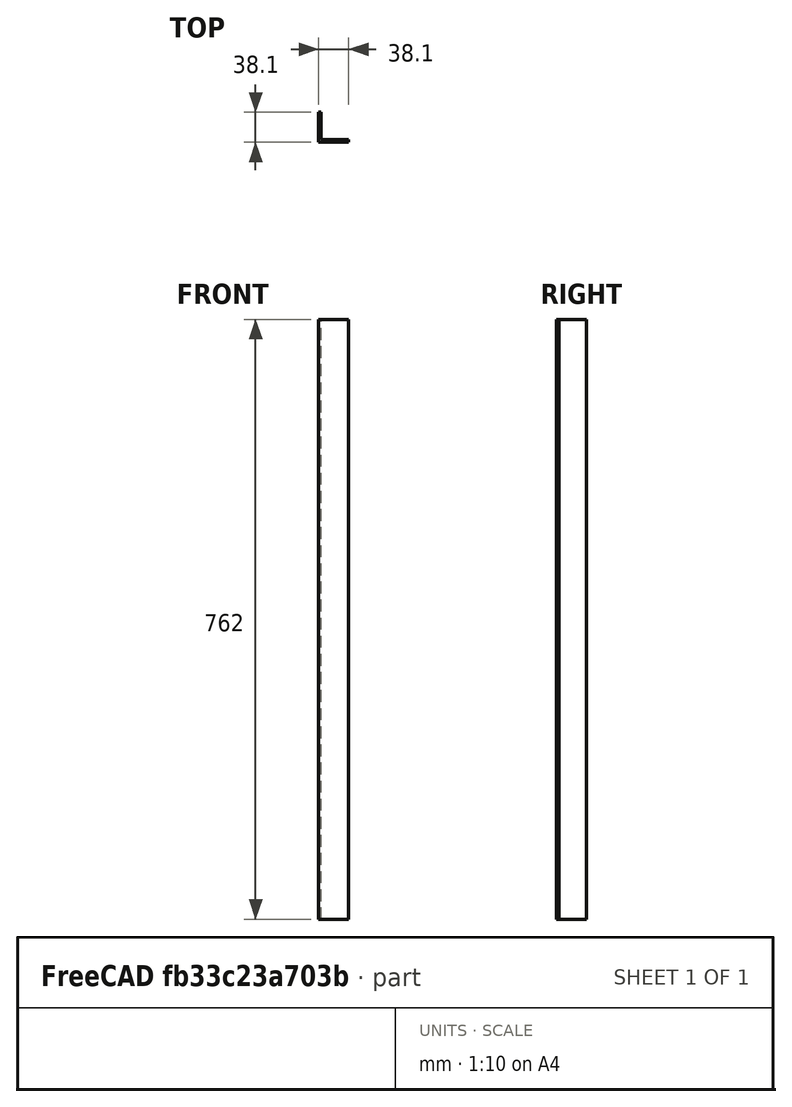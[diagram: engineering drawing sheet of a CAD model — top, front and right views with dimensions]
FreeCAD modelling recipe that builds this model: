
FCSTD DOCUMENT  (FreeCAD 0.20R29603 (Git))
Label: Angle - 30in
License: All rights reserved
LicenseURL: http://en.wikipedia.org/wiki/All_rights_reserved
objects: Sketcher::SketchObject×1, PartDesign::Pad×1
note: 3 computed .brp shape members not serialized (recipe doc carries the construction recipe); baked Part::Feature solids carry a one-line shape summary decoded from their .brp

FEATURE [Sketcher::SketchObject] Sketch
  FullyConstrained = false
  MapMode = 5
  sketch-geometry (6):
    g0: LineSegment StartX=0 StartY=0 StartZ=0 EndX=38.1 EndY=0 EndZ=0
    g1: LineSegment StartX=38.1 StartY=0 StartZ=0 EndX=38.1 EndY=3.175 EndZ=0
    g2: LineSegment StartX=38.1 StartY=3.175 StartZ=0 EndX=3.175 EndY=3.175 EndZ=0
    g3: LineSegment StartX=3.175 StartY=3.175 StartZ=0 EndX=3.175 EndY=38.1 EndZ=0
    g4: LineSegment StartX=3.175 StartY=38.1 StartZ=0 EndX=0 EndY=38.1 EndZ=0
    g5: LineSegment StartX=0 StartY=38.1 StartZ=0 EndX=0 EndY=0 EndZ=0
  constraints (17):
    c: Coincident(g-1,g0)
    c: PointOnObject(g0,g-1)
    c: Coincident(g0,g1)
    c: Vertical(g1)
    c: Coincident(g1,g2)
    c: Horizontal(g2)
    c: Coincident(g2,g3)
    c: Vertical(g3)
    c: Coincident(g3,g4)
    c: PointOnObject(g4,g-2)
    c: Coincident(g4,g5)
    c: Coincident(g5,g0)
    c: Horizontal(g4)
    c: Equal(g1,g4)
    c: Equal(g0,g5)
    c: Distance(g0) = 38.1
    c: DistanceY(g1,g1) = 3.175
FEATURE [PartDesign::Pad] Pad  label="Angle - 30in"
  AllowMultiFace = false
  Direction = (0,0,1)
  Length = 762
  Length2 = 100
  Profile = -> Sketch
  ReferenceAxis = -> Sketch [N_Axis]
  Type = 0
